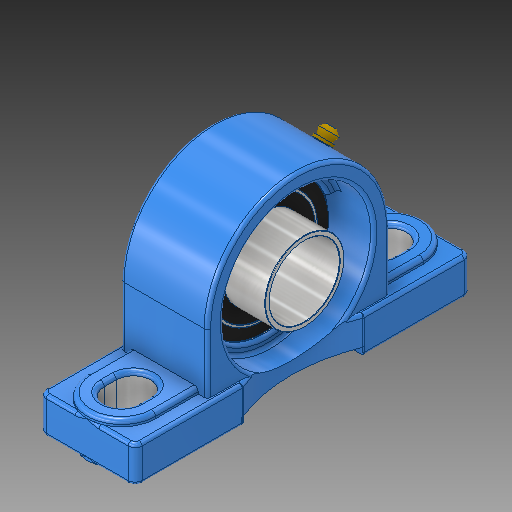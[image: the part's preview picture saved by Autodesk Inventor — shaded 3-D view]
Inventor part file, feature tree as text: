
AUTODESK INVENTOR PART (.ipt)
format: ipt  version: 2019 (Build 230136000, 136)  size: 681,984 bytes
history: native  units: in
note: dims shown in document units (in); Inventor stores cm internally (conversion verified against a paired STEP export)
features: sketch x28, plane x7, other x3
ambient origin geometry x8: Origin, YZ Plane, XZ Plane, XY Plane, X Axis, Y Axis, Z Axis, Center Point
bodies: Solid1 (feature_tree)
feature tree (38):
  other  "Pillow Bearing inventor_MIR2.ipt"
  other  "Solid1::Pillow Bearing inventor_MIR2.ipt"
  other  "TaggingFeature1"
  sketch  "Sketch1"  dims[d0=0.3937in]
  sketch  "Sketch2"
  sketch  "Sketch3"
  sketch  "Sketch4"
  sketch  "Sketch5"
  sketch  "Sketch6"
  sketch  "Sketch7"
  sketch  "Sketch8"
  sketch  "Sketch9"
  sketch  "Sketch10"
  sketch  "Sketch11"
  sketch  "Sketch13"
  sketch  "Sketch14"
  sketch  "Sketch15"
  sketch  "Sketch17"
  sketch  "Sketch18"
  sketch  "Sketch19"
  sketch  "Sketch20"
  sketch  "Sketch21"
  sketch  "Sketch22"
  sketch  "Sketch23"
  sketch  "Sketch24"
  sketch  "Sketch25"
  sketch  "Sketch26"
  sketch  "Sketch27"
  sketch  "Sketch28"
  sketch  "Sketch29"
  sketch  "Sketch30"
  plane  "Work Plane1"
  plane  "Work Plane2"
  plane  "Work Plane5"
  plane  "Work Plane6"
  plane  "Work Plane7"
  plane  "Work Plane8"
  plane  "Work Plane9"
